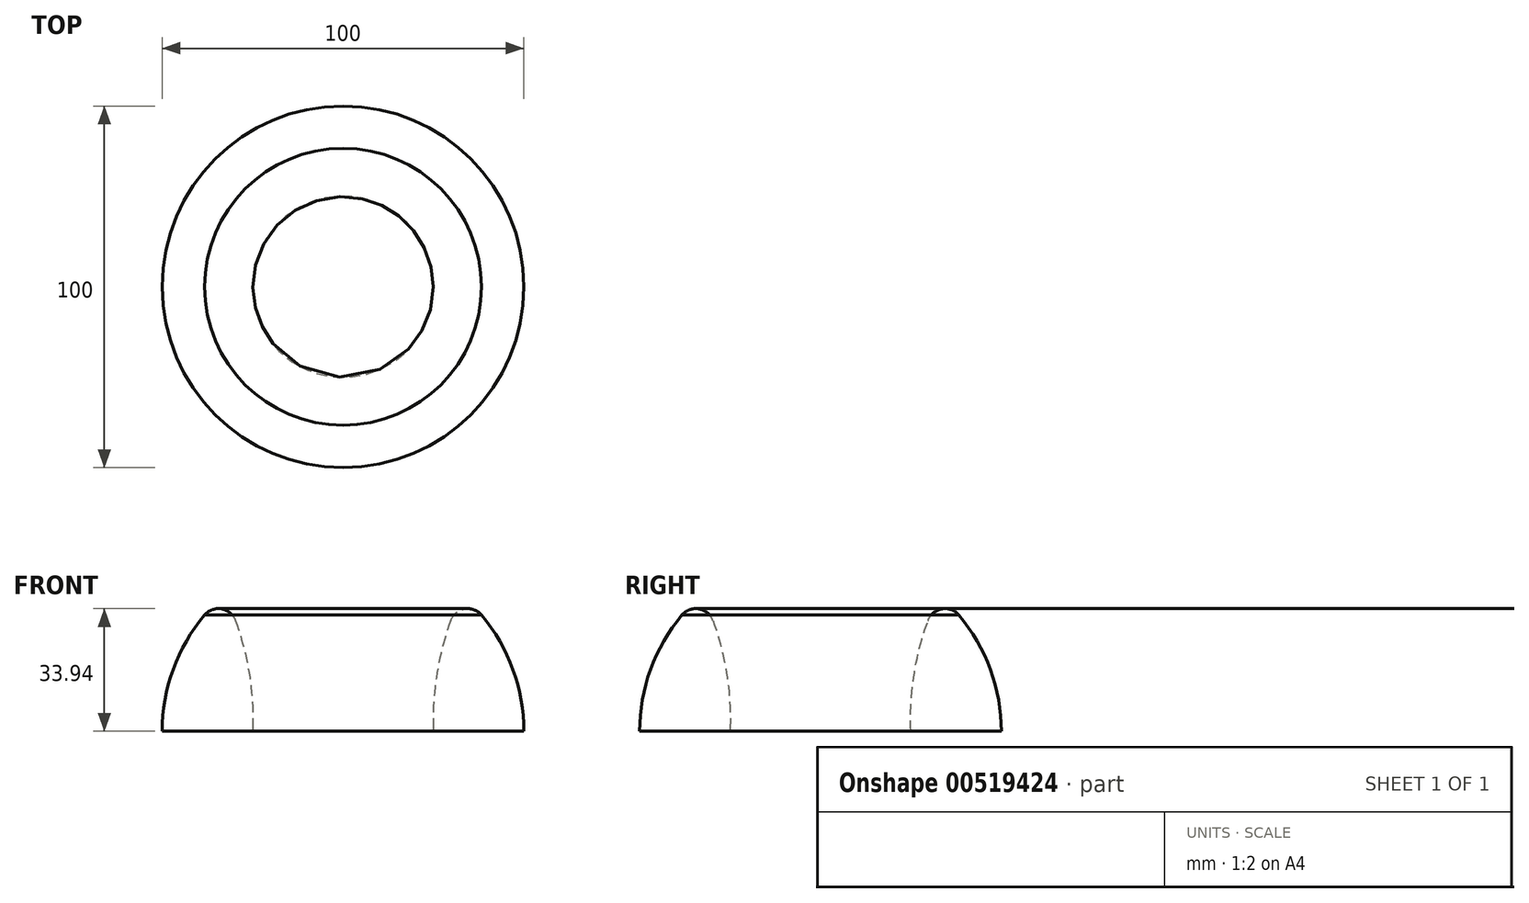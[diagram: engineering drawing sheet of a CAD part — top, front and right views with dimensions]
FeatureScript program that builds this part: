
annotation { "Feature Type Name" : "Feature", "Feature Type Description" : "" }
export const myFeature = defineFeature(function(context is Context, id is Id, definition is map)
    precondition{}
    {
        {
            var Q0;
            Q0=qCreatedBy(makeId("Top.planeOp"),FACE);
            var sketch = newSketch(context, id + "F0", { "sketchPlane" : qUnion([Q0])});
            skArc(sketch, "E0", {"start": v(0, 50) * mm, "mid": v(-50, 0) * mm, "end": v(0, -50) * mm});
            skLineSegment(sketch, "E1", {"start": v(0, 50) * mm, "end": v(0, -50) * mm});
            skSolve(sketch);
        }
        {
            var Q0;
            Q0=makeQuery(id+"F0.imprint","IMPRINT",FACE,{"disambiguationData":[TD([[makeQuery(id+"F0.imprint","IMPRINT",EDGE,{"derivedFrom":sQuery(id+"F0.wireOp",EDGE,"E0")}),1.0]])]});
            var Q1;
            Q1=sQuery(id+"F0.wireOp",EDGE,"E1");
            revolve(context, id + "F1", {"entities" : qUnion([Q0]), "axis" : qUnion([Q1]), "revolveType" : RevolveType.ONE_DIRECTION, "oppositeDirection" : true, "angle" : 180 * degree});
        }
        {
            var Q0;
            Q0=qCreatedBy(makeId("Top.planeOp"),FACE);
            cPlane(context, id + "F2", {"entities" : qUnion([Q0]), "cplaneType" : CPlaneType.OFFSET, "offset" : 50 * mm, "width" : 150 * mm, "height" : 150 * mm});
        }
        {
            var Q0;
            Q0=qCreatedBy(id+"F2.planeOp",FACE);
            var sketch = newSketch(context, id + "F3", { "sketchPlane" : qUnion([Q0])});
            skCircle(sketch, "E2", {"center": v(0, 0) * mm, "radius": 40 * mm});
            skSolve(sketch);
        }
        {
            var Q0;
            Q0=qCreatedBy(makeId("Top.planeOp"),FACE);
            var sketch = newSketch(context, id + "F4", { "sketchPlane" : qUnion([Q0])});
            skCircle(sketch, "E3", {"center": v(0, 0) * mm, "radius": 25 * mm});
            skSolve(sketch);
        }
        {
            var Q0;
            Q0=qCreatedBy(makeId("Front.planeOp"),FACE);
            var sketch = newSketch(context, id + "F5", { "sketchPlane" : qUnion([Q0])});
            skArc(sketch, "E4", {"start": v(40, 50) * mm, "mid": v(28.3, 26.26) * mm, "end": v(25, 0) * mm});
            skSolve(sketch);
        }
        {
            var Q1;
            Q1=makeQuery(id+"F3.imprint","IMPRINT",FACE,{"disambiguationData":[TD([[makeQuery(id+"F3.imprint","IMPRINT",EDGE,{"derivedFrom":sQuery(id+"F3.wireOp",EDGE,"E2")}),1.0]])]});
            var Q2;
            Q2=makeQuery(id+"F4.imprint","IMPRINT",FACE,{"disambiguationData":[TD([[makeQuery(id+"F4.imprint","IMPRINT",EDGE,{"derivedFrom":sQuery(id+"F4.wireOp",EDGE,"E3")}),1.0]])]});
            var Q3;
            Q3=sQuery(id+"F5.wireOp",EDGE,"E4");
            loft(context, id + "F6", {"operationType" : NewBodyOperationType.REMOVE, "addGuides" : true, "sheetProfilesArray" : [{ "sheetProfileEntities" : qUnion([Q1]) }, { "sheetProfileEntities" : qUnion([Q2]) }], "guidesArray" : [{ "guideEntities" : qUnion([Q3]), "guideDerivativeType" : LoftGuideDerivativeType.DEFAULT, "guideDerivativeMagnitude" : 1 }]});
        }
        {
            var Q0;
            Q0=makeQuery(id+"F6.boolean.opBoolean","INTERSECT",EDGE,{"derivedFrom":[makeQuery(id+"F1.opRevolve","SWEPT_FACE",FACE,{"disambiguationData":[OSD([sQuery(id+"F0.wireOp",EDGE,"E0")])]}),makeQuery(id+"F6.opLoft","SWEPT_FACE",FACE,{"disambiguationData":[OSD([sQuery(id+"F3.wireOp",EDGE,"E2"),sQuery(id+"F4.wireOp",EDGE,"E3"),sQuery(id+"F5.wireOp",EDGE,"E4")])]})]});
            fillet(context, id + "F7", {"entities" : qUnion([Q0]), "radius" : 5 * mm, "tangentPropagation" : true, "allowEdgeOverflow" : false});
        }
    });
